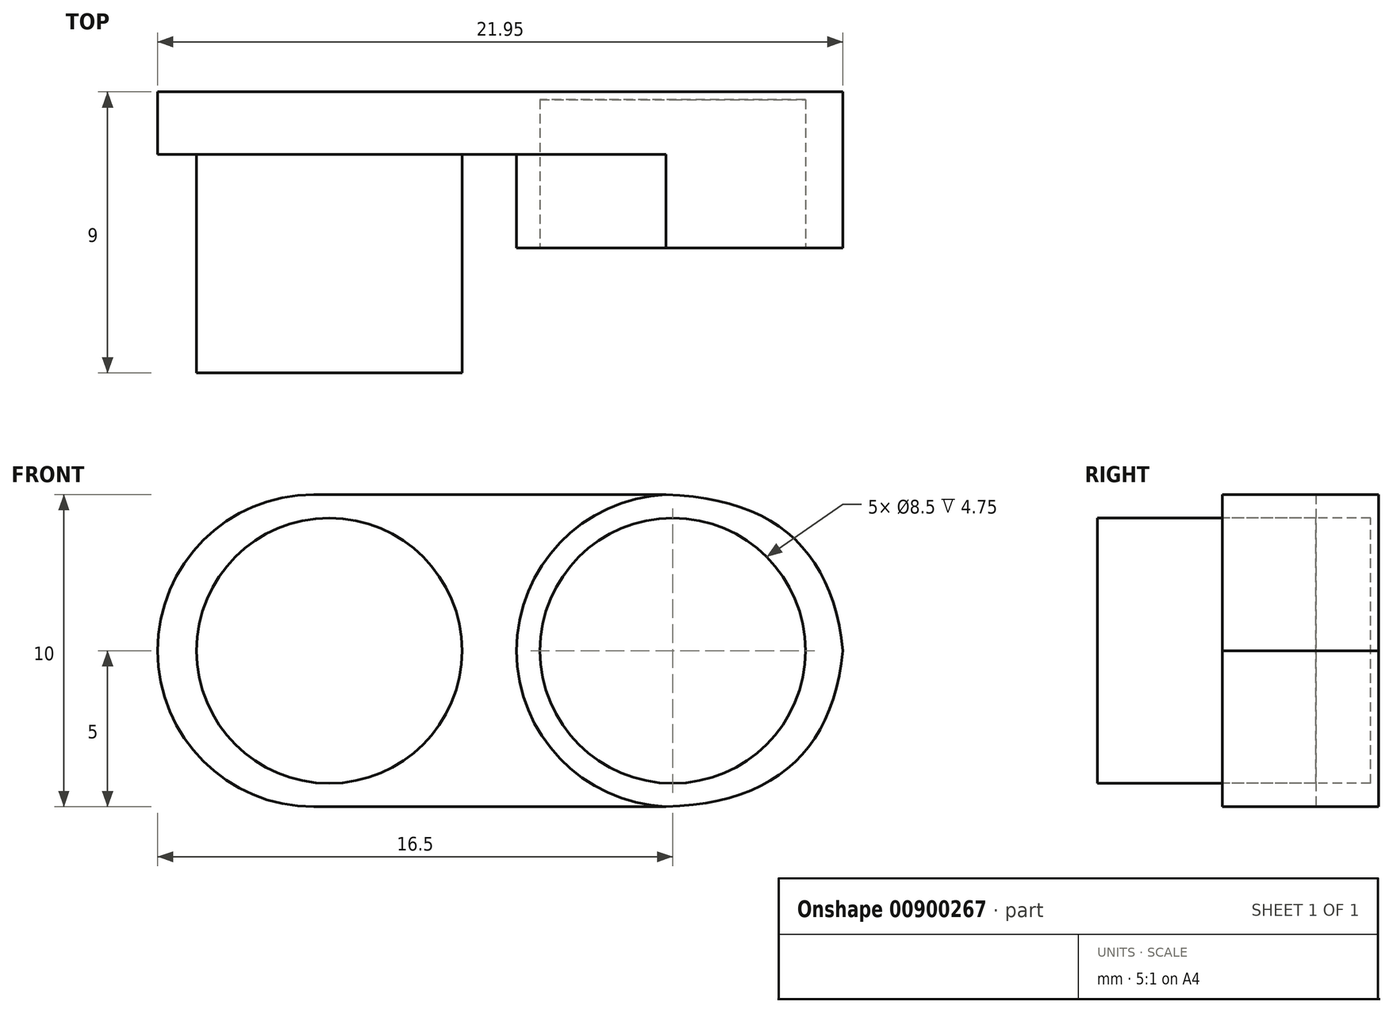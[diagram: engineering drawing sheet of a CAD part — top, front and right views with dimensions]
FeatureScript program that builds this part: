
annotation { "Feature Type Name" : "Feature", "Feature Type Description" : "" }
export const myFeature = defineFeature(function(context is Context, id is Id, definition is map)
    precondition{}
    {
        {
            var Q0;
            Q0=qCreatedBy(makeId("Top.planeOp"),FACE);
            var sketch = newSketch(context, id + "F0", { "sketchPlane" : qUnion([Q0])});
            skLineSegment(sketch, "E0.bottom", {"start": v(-11, 2.5) * mm, "end": v(11, 2.5) * mm});
            skLineSegment(sketch, "E0.top", {"start": v(-11, -6.5) * mm, "end": v(11, -6.5) * mm});
            skLineSegment(sketch, "E0.left", {"start": v(-11, 2.5) * mm, "end": v(-11, -6.5) * mm});
            skLineSegment(sketch, "E0.right", {"start": v(11, 2.5) * mm, "end": v(11, -6.5) * mm});
            skSolve(sketch);
        }
        {
            var Q0;
            Q0 = qSketchRegion(id + "F0", true);
            extrude(context, id + "F1", {"entities" : qUnion([Q0]), "depth" : 10 * mm, "offsetDistance" : 25 * mm});
        }
        {
            var Q0;
            Q0=makeQuery(id+"F1.opExtrude","SWEPT_FACE",FACE,{"disambiguationData":[OSD([sQuery(id+"F0.wireOp",EDGE,"E0.top")])]});
            var sketch = newSketch(context, id + "F2", { "sketchPlane" : qUnion([Q0])});
            skLineSegment(sketch, "E1", {"start": v(0, 0) * mm, "end": v(0, 10) * mm});
            skSolve(sketch);
        }
        {
            var Q0;
            Q0 = qSketchRegion(id + "F2", true);
            var Q1;
            {var subQ0=sQuery(id+"F2.wireOp",EDGE,"E1");Q1=makeQuery(id+"F2.imprint","IMPRINT",FACE,{"disambiguationData":[TD([[makeQuery(id+"F2.imprint","IMPRINT",EDGE,{"derivedFrom":subQ0}),-1.0]])]});}
            extrude(context, id + "F3", {"entities" : qUnion([Q0, Q1]), "operationType" : NewBodyOperationType.REMOVE, "oppositeDirection" : true, "depth" : 4 * mm, "offsetDistance" : 25 * mm});
        }
        {
            var Q0;
            Q0=makeQuery(id+"F3.boolean.opBoolean","COPY",FACE,{"derivedFrom":makeQuery(id+"F3.opExtrude","CAP_FACE",FACE,{"disambiguationData":[OSD([sQuery(id+"F0.wireOp",EDGE,"E0.top"),sQuery(id+"F0.wireOp",EDGE,"E0.right"),sQuery(id+"F2.wireOp",EDGE,"E1")])],"isStart":false})});
            var sketch = newSketch(context, id + "F4", { "sketchPlane" : qUnion([Q0])});
            skCircle(sketch, "E2", {"center": v(5.5, 5) * mm, "radius": 5 * mm});
            skSolve(sketch);
        }
        {
            var Q0;
            {var subQ4=sQuery(id+"F2.wireOp",EDGE,"E1");var subQ10=makeQuery(id+"F3.boolean.opBoolean","COPY",EDGE,{"derivedFrom":makeQuery(id+"F3.opExtrude","CAP_EDGE",EDGE,{"disambiguationData":[OSD([subQ4])],"isStart":false})});Q0=makeQuery(id+"F4.imprint","IMPRINT",FACE,{"disambiguationData":[TD([[makeQuery(id+"F4.imprint","IMPRINT",EDGE,{"derivedFrom":subQ10}),-1.0]])]});}
            var Q1;
            {var subQ1=sQuery(id+"F0.wireOp",EDGE,"E0.top");var subQ3=sQuery(id+"F0.wireOp",EDGE,"E0.right");var subQ11=makeQuery(id+"F3.boolean.opBoolean","COPY",EDGE,{"derivedFrom":makeQuery(id+"F3.opExtrude","CAP_EDGE",EDGE,{"disambiguationData":[OSD([subQ1,subQ3])],"isStart":false})});Q1=makeQuery(id+"F4.imprint","IMPRINT",FACE,{"disambiguationData":[TD([[makeQuery(id+"F4.imprint","IMPRINT",EDGE,{"derivedFrom":subQ11}),-1.0]])]});}
            extrude(context, id + "F5", {"entities" : qUnion([Q0, Q1]), "operationType" : NewBodyOperationType.REMOVE, "oppositeDirection" : true, "depth" : 3 * mm, "offsetDistance" : 25 * mm});
        }
        {
            var Q0;
            Q0=makeQuery(id+"F3.boolean.opBoolean","COPY",FACE,{"derivedFrom":makeQuery(id+"F3.opExtrude","CAP_FACE",FACE,{"disambiguationData":[OSD([sQuery(id+"F0.wireOp",EDGE,"E0.top"),sQuery(id+"F0.wireOp",EDGE,"E0.right"),sQuery(id+"F2.wireOp",EDGE,"E1")])],"isStart":false})});
            var sketch = newSketch(context, id + "F6", { "sketchPlane" : qUnion([Q0])});
            skCircle(sketch, "E3", {"center": v(5.5, 5) * mm, "radius": 4.25 * mm});
            skSolve(sketch);
        }
        {
            var Q0;
            Q0=makeQuery(id+"F6.imprint","IMPRINT",FACE,{"disambiguationData":[TD([[makeQuery(id+"F6.imprint","IMPRINT",EDGE,{"derivedFrom":sQuery(id+"F6.wireOp",EDGE,"E3")}),1.0]])]});
            extrude(context, id + "F7", {"entities" : qUnion([Q0]), "operationType" : NewBodyOperationType.REMOVE, "oppositeDirection" : true, "depth" : 4.75 * mm, "offsetDistance" : 25 * mm});
        }
        {
            var Q0;
            Q0=makeQuery(id+"F1.opExtrude","SWEPT_FACE",FACE,{"disambiguationData":[OSD([sQuery(id+"F0.wireOp",EDGE,"E0.top")])]});
            var sketch = newSketch(context, id + "F8", { "sketchPlane" : qUnion([Q0])});
            skCircle(sketch, "E4", {"center": v(-5.5, 5) * mm, "radius": 4.25 * mm});
            skSolve(sketch);
        }
        {
            var Q0;
            Q0=makeQuery(id+"F8.imprint","IMPRINT",FACE,{"disambiguationData":[TD([[makeQuery(id+"F8.imprint","IMPRINT",EDGE,{"derivedFrom":sQuery(id+"F8.wireOp",EDGE,"E4")}),-1.0]])]});
            extrude(context, id + "F9", {"entities" : qUnion([Q0]), "operationType" : NewBodyOperationType.REMOVE, "oppositeDirection" : true, "depth" : 7 * mm, "offsetDistance" : 25 * mm});
        }
        {
            var Q0;
            Q0=makeQuery(id+"F1.opExtrude","CAP_EDGE",EDGE,{"disambiguationData":[OSD([sQuery(id+"F0.wireOp",EDGE,"E0.right")])],"isStart":true});
            var Q1;
            Q1=makeQuery(id+"F1.opExtrude","CAP_EDGE",EDGE,{"disambiguationData":[OSD([sQuery(id+"F0.wireOp",EDGE,"E0.right")])],"isStart":false});
            fillet(context, id + "F10", {"entities" : qUnion([Q0, Q1]), "radius" : 6.04 * mm, "rho" : 0.5, "crossSection" : FilletCrossSection.CONIC, "allowEdgeOverflow" : false});
        }
        {
            var Q0;
            Q0=makeQuery(id+"F1.opExtrude","CAP_EDGE",EDGE,{"disambiguationData":[OSD([sQuery(id+"F0.wireOp",EDGE,"E0.left")])],"isStart":false});
            var Q1;
            Q1=makeQuery(id+"F1.opExtrude","CAP_EDGE",EDGE,{"disambiguationData":[OSD([sQuery(id+"F0.wireOp",EDGE,"E0.left")])],"isStart":true});
            fillet(context, id + "F11", {"entities" : qUnion([Q0, Q1]), "radius" : 5 * mm, "tangentPropagation" : true, "allowEdgeOverflow" : false});
        }
    });
